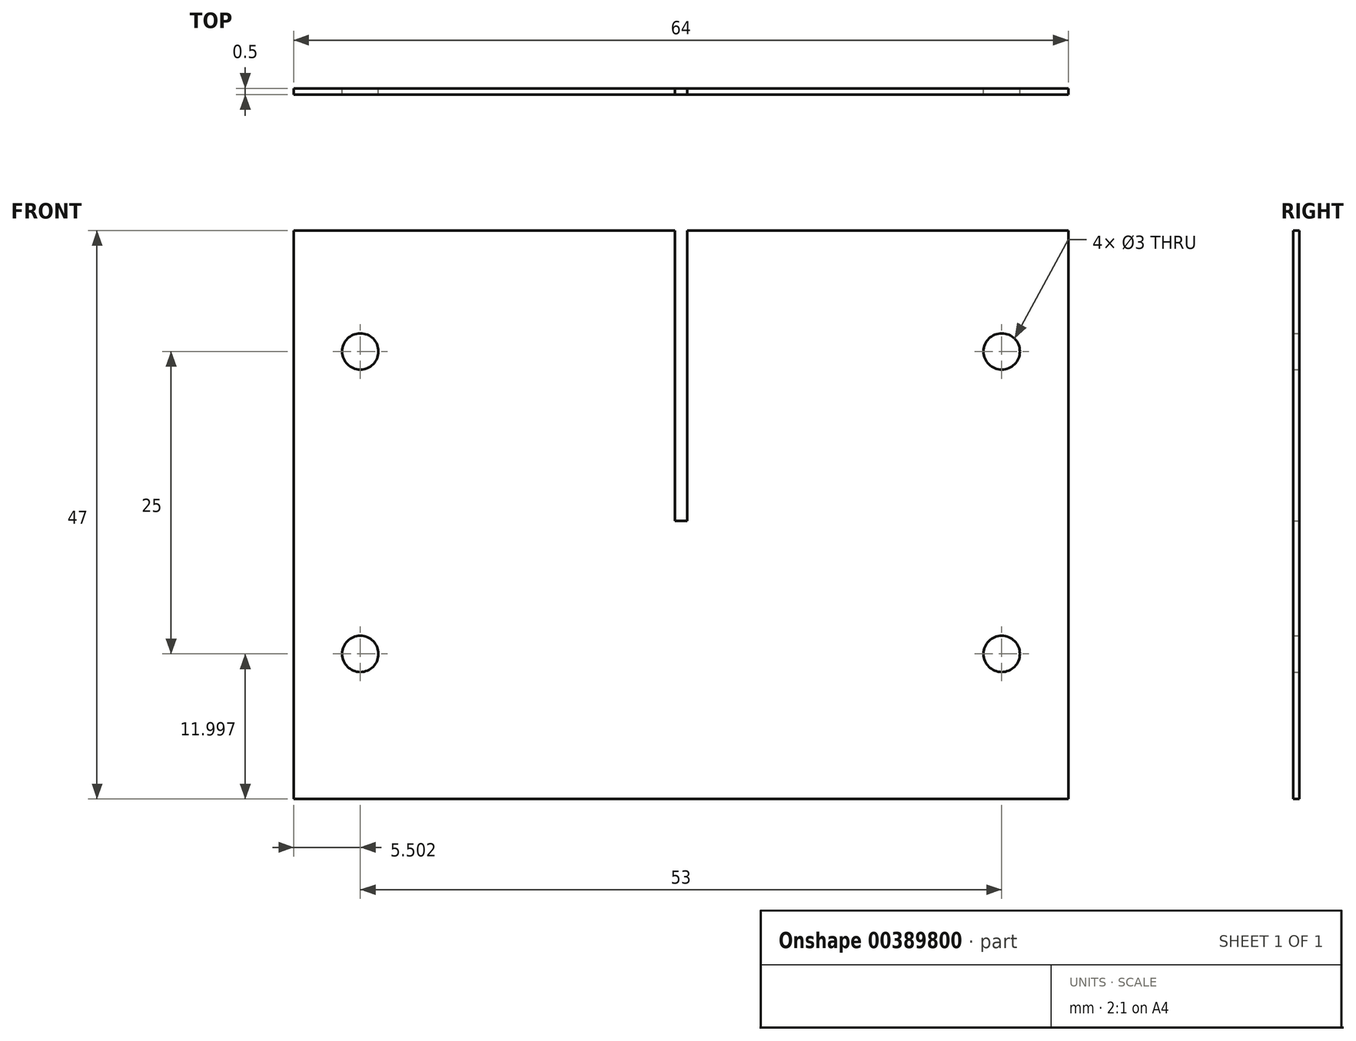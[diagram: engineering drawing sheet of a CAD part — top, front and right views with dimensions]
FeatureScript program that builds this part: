
annotation { "Feature Type Name" : "Feature", "Feature Type Description" : "" }
export const myFeature = defineFeature(function(context is Context, id is Id, definition is map)
    precondition{}
    {
        {
            var Q0;
            Q0=qCreatedBy(makeId("Front.planeOp"),FACE);
            var sketch = newSketch(context, id + "F0", { "sketchPlane" : qUnion([Q0])});
            skLineSegment(sketch, "E0.top", {"start": v(-47.57, -30.43) * mm, "end": v(16.43, -30.43) * mm});
            skLineSegment(sketch, "E0.left", {"start": v(-47.57, 16.57) * mm, "end": v(-47.57, -30.43) * mm});
            skLineSegment(sketch, "E0.right", {"start": v(16.43, 16.57) * mm, "end": v(16.43, -30.43) * mm});
            skLineSegment(sketch, "E1", {"start": v(-37.57, 16.57) * mm, "end": v(-37.57, -30.43) * mm});
            skLineSegment(sketch, "E2", {"start": v(6.43, 16.57) * mm, "end": v(6.43, -30.43) * mm});
            skCircle(sketch, "E3", {"center": v(-42.07, 6.57) * mm, "radius": 1.5 * mm});
            skCircle(sketch, "E4", {"center": v(-42.07, -18.43) * mm, "radius": 1.5 * mm});
            skCircle(sketch, "E5", {"center": v(10.93, 6.57) * mm, "radius": 1.5 * mm});
            skCircle(sketch, "E6", {"center": v(10.93, -18.43) * mm, "radius": 1.5 * mm});
            skLineSegment(sketch, "E7", {"start": v(-16.07, 16.57) * mm, "end": v(-16.07, -7.43) * mm});
            skLineSegment(sketch, "E8", {"start": v(-16.07, -7.43) * mm, "end": v(-15.07, -7.43) * mm});
            skLineSegment(sketch, "E9", {"start": v(-15.07, -7.43) * mm, "end": v(-15.07, 16.57) * mm});
            skLineSegment(sketch, "E10", {"start": v(-47.57, 16.57) * mm, "end": v(-37.57, 16.57) * mm});
            skLineSegment(sketch, "E11", {"start": v(-37.57, 16.57) * mm, "end": v(-16.07, 16.57) * mm});
            skLineSegment(sketch, "E12", {"start": v(-15.07, 16.57) * mm, "end": v(6.43, 16.57) * mm});
            skLineSegment(sketch, "E13", {"start": v(6.43, 16.57) * mm, "end": v(16.43, 16.57) * mm});
            skSolve(sketch);
        }
        {
            var Q0;
            Q0 = qSketchRegion(id + "F0", true);
            extrude(context, id + "F1", {"entities" : qUnion([Q0]), "depth" : 0.5 * mm});
        }
    });
